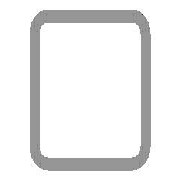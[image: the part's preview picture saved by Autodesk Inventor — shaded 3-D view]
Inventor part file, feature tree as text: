
AUTODESK INVENTOR PART (.ipt)
format: ipt  version: 2025 (Build 290162010, 162A)  size: 138,752 bytes
history: native  units: mm (DEFAULTED — no unit token found)
features: other x4, sketch x1, plane x1
ambient origin geometry x8: Origin, YZ Plane, XZ Plane, XY Plane, X Axis, Y Axis, Z Axis, Center Point
bodies: Solid1 (feature_tree), Body (feature_tree)
feature tree (6):
  parser-record x1  (decoder bookkeeping rows leaked as tree rows — omitted from the tree; the rows remain in map.json)
  other  "Driven Length"
  other  "Start Plane"
  other  "End Plane"
  sketch  "Sketch3"  dims[d3=1800.0mm d4=0.0mm d7=4.5mm d10=80.0mm d11=80.0mm d12=3.0mm d13=-0.0mm d14=1800.0mm d15=40.0mm d16=40.0mm d17=90.0deg d18=1800.0mm]
  plane  "Work Plane3"
